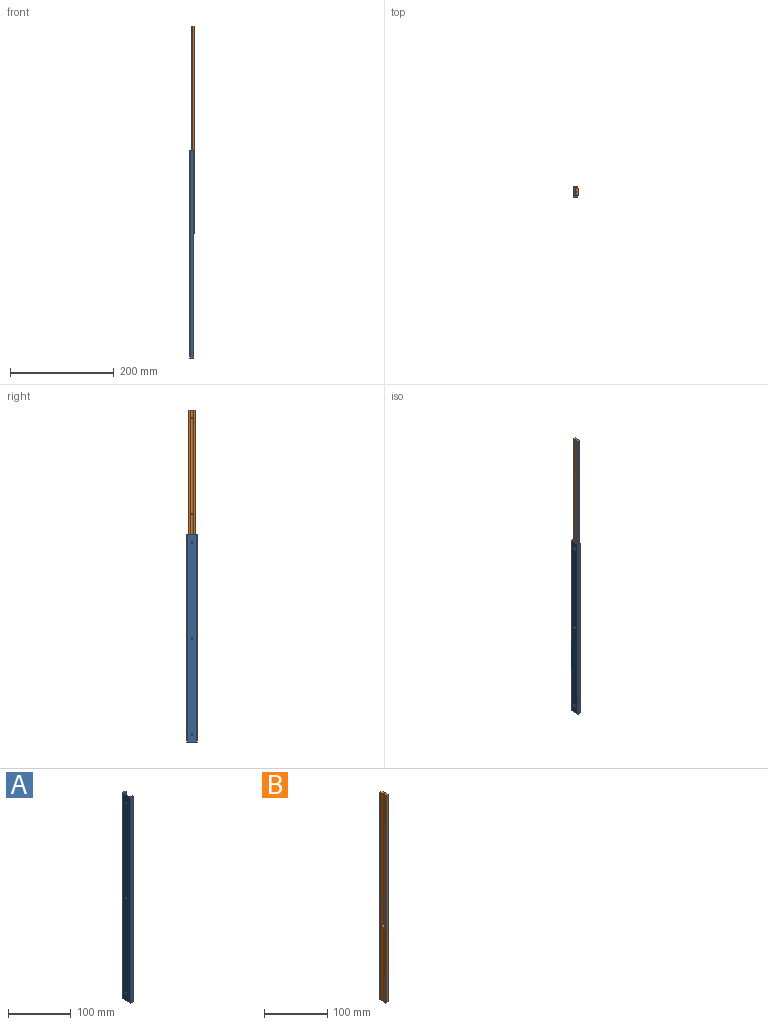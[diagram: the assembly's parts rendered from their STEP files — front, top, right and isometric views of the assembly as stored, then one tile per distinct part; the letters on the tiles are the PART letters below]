
ASSEMBLY  parts=2 mates=1
PART A: 163 faces, bbox 7.6x20.2x400.2 mm
  f0: sphere r=1.2mm, area 2.1mm2, adj f72,f125,f160,f161
  f1: sphere r=1.2mm, area 2.1mm2, adj f72,f125,f158,f159
  f2: sphere r=1.2mm, area 2.1mm2, adj f72,f125,f157,f158
  f3: sphere r=1.2mm, area 2.1mm2, adj f72,f125,f156,f157
  f4: sphere r=1.2mm, area 2.1mm2, adj f72,f125,f155,f156
  f5: sphere r=1.2mm, area 2.1mm2, adj f72,f125,f154,f155
  f6: sphere r=1.2mm, area 2.1mm2, adj f72,f125,f153,f154
  f7: sphere r=1.2mm, area 2.1mm2, adj f72,f125,f152,f153
  f8: sphere r=1.2mm, area 2.1mm2, adj f72,f125,f151,f152
  f9: sphere r=1.2mm, area 2.1mm2, adj f72,f125,f150,f151
  f10: sphere r=1.2mm, area 2.1mm2, adj f72,f125,f149,f150
  f11: sphere r=1.2mm, area 2.1mm2, adj f72,f125,f148,f149
  f12: sphere r=1.2mm, area 2.1mm2, adj f72,f125,f147,f148
  f13: sphere r=1.2mm, area 2.1mm2, adj f72,f125,f146,f147
  f14: sphere r=1.2mm, area 2.1mm2, adj f72,f125,f145,f146
  f15: sphere r=1.2mm, area 2.1mm2, adj f72,f125,f144,f145
  f16: sphere r=1.2mm, area 2.1mm2, adj f72,f125,f143,f144
  f17: sphere r=1.2mm, area 2.1mm2, adj f72,f125,f142,f143
  f18: sphere r=1.2mm, area 2.1mm2, adj f72,f125,f141,f142
  f19: sphere r=1.2mm, area 2.1mm2, adj f72,f125,f140,f141
  f20: sphere r=1.2mm, area 2.1mm2, adj f72,f125,f139,f140
  f21: sphere r=1.2mm, area 2.1mm2, adj f72,f125,f138,f139
  f22: sphere r=1.2mm, area 2.1mm2, adj f72,f125,f137,f138
  f23: sphere r=1.2mm, area 2.1mm2, adj f72,f125,f136,f137
  f24: sphere r=1.2mm, area 2.1mm2, adj f72,f125,f135,f136
  f25: sphere r=1.2mm, area 2.1mm2, adj f72,f125,f134,f135
  f26: sphere r=1.2mm, area 2.1mm2, adj f72,f125,f133,f134
  f27: sphere r=1.2mm, area 2.1mm2, adj f72,f125,f132,f133
  f28: sphere r=1.2mm, area 2.1mm2, adj f72,f125,f131,f132
  f29: sphere r=1.2mm, area 2.1mm2, adj f72,f125,f130,f131
  f30: sphere r=1.2mm, area 2.1mm2, adj f72,f125,f129,f130
  f31: sphere r=1.2mm, area 2.1mm2, adj f72,f125,f128,f129
  f32: sphere r=1.2mm, area 2.1mm2, adj f72,f125,f127,f128
  f33: sphere r=1.2mm, area 2.1mm2, adj f72,f125,f126,f127
  f34: sphere r=1.2mm, area 2.1mm2, adj f72,f125,f126,f160
  f35: sphere r=1.2mm, area 2.1mm2, adj f77,f83,f119,f120
  f36: sphere r=1.2mm, area 2.1mm2, adj f77,f83,f117,f118
  f37: sphere r=1.2mm, area 2.1mm2, adj f77,f83,f116,f117
  f38: sphere r=1.2mm, area 2.1mm2, adj f77,f83,f115,f116
  f39: sphere r=1.2mm, area 2.1mm2, adj f77,f83,f114,f115
  f40: sphere r=1.2mm, area 2.1mm2, adj f77,f83,f113,f114
  f41: sphere r=1.2mm, area 2.1mm2, adj f77,f83,f112,f113
  f42: sphere r=1.2mm, area 2.1mm2, adj f77,f83,f111,f112
  f43: sphere r=1.2mm, area 2.1mm2, adj f77,f83,f110,f111
  f44: sphere r=1.2mm, area 2.1mm2, adj f77,f83,f109,f110
  f45: sphere r=1.2mm, area 2.1mm2, adj f77,f83,f108,f109
  f46: sphere r=1.2mm, area 2.1mm2, adj f77,f83,f107,f108
  f47: sphere r=1.2mm, area 2.1mm2, adj f77,f83,f106,f107
  f48: sphere r=1.2mm, area 2.1mm2, adj f77,f83,f105,f106
  f49: sphere r=1.2mm, area 2.1mm2, adj f77,f83,f104,f105
  f50: sphere r=1.2mm, area 2.1mm2, adj f77,f83,f103,f104
  f51: sphere r=1.2mm, area 2.1mm2, adj f77,f83,f102,f103
  f52: sphere r=1.2mm, area 2.1mm2, adj f77,f83,f101,f102
  f53: sphere r=1.2mm, area 2.1mm2, adj f77,f83,f100,f101
  f54: sphere r=1.2mm, area 2.1mm2, adj f77,f83,f99,f100
  f55: sphere r=1.2mm, area 2.1mm2, adj f77,f83,f98,f99
  f56: sphere r=1.2mm, area 2.1mm2, adj f77,f83,f97,f98
  f57: sphere r=1.2mm, area 2.1mm2, adj f77,f83,f96,f97
  f58: sphere r=1.2mm, area 2.1mm2, adj f77,f83,f95,f96
  f59: sphere r=1.2mm, area 2.1mm2, adj f77,f83,f94,f95
  f60: sphere r=1.2mm, area 2.1mm2, adj f77,f83,f93,f94
  f61: sphere r=1.2mm, area 2.1mm2, adj f77,f83,f92,f93
  f62: sphere r=1.2mm, area 2.1mm2, adj f77,f83,f91,f92
  f63: sphere r=1.2mm, area 2.1mm2, adj f77,f83,f90,f91
  f64: sphere r=1.2mm, area 2.1mm2, adj f77,f83,f89,f90
  f65: sphere r=1.2mm, area 2.1mm2, adj f77,f83,f88,f89
  f66: sphere r=1.2mm, area 2.1mm2, adj f77,f83,f87,f88
  f67: sphere r=1.2mm, area 2.1mm2, adj f77,f83,f86,f87
  f68: sphere r=1.2mm, area 2.1mm2, adj f77,f83,f85,f86
  f69: sphere r=1.2mm, area 2.1mm2, adj f77,f83,f84,f85
  f70: sphere r=1.2mm, area 2.1mm2, adj f77,f83,f84,f119
  f71: sphere r=1.2mm, area 2.1mm2, adj f72,f125,f159,f162
  f72: plane 400.25x1.51mm, normal (0,1,0), area 504mm2, adj f0,f1,f2,f3,f4,f5,f6,f7
  f73: plane 20x7.4mm, normal (0,0,1), area 56.3mm2, adj f72,f74,f75,f76,f77,f79,f80,f82
  f74: plane 400x0.71mm, normal (-0.71,0.71,0), area 400mm2, adj f73,f75,f78,f80
  f75: plane 400x6.69mm, normal (0,1,0), area 2677.2mm2, adj f73,f74,f76,f78
  f76: plane 400x2.5mm, normal (1,0,0), area 1000mm2, adj f73,f75,f77,f78
  f77: plane 400.25x3.11mm, normal (0,-1,0), area 1144mm2, adj f35,f36,f37,f38,f39,f40,f41,f42
  f78: plane 20x7.4mm, normal (0,0,-1), area 56.3mm2, adj f72,f74,f75,f76,f77,f79,f80,f82
  f79: plane 400x0.71mm, normal (-0.71,-0.71,0), area 400mm2, adj f73,f78,f80,f123
  f80: plane 400x18.59mm, normal (-1,0,0), area 7408.7mm2, adj f73,f74,f78,f79,f81,f121,f122
  f81: cone r=1.65mm half-angle=45deg, axis (1,0,0), area 29.2mm2, adj f80,f82
  f82: plane 400x15mm, normal (1,0,0), area 5912.3mm2, adj f72,f73,f78,f81,f83,f121,f122
  f83: plane 400.25x1.51mm, normal (0,-1,0), area 504mm2, adj f35,f36,f37,f38,f39,f40,f41,f42
  f84: cylinder r=1.2mm len=2.51mm, axis (0,0,1), area 5.2mm2, adj f69,f70,f77,f83
  f85: cylinder r=1.2mm len=2.51mm, axis (0,0,1), area 5.2mm2, adj f68,f69,f77,f83
  f86: cylinder r=1.2mm len=2.51mm, axis (0,0,1), area 5.2mm2, adj f67,f68,f77,f83
  f87: cylinder r=1.2mm len=2.51mm, axis (0,0,1), area 5.2mm2, adj f66,f67,f77,f83
  f88: cylinder r=1.2mm len=2.51mm, axis (0,0,1), area 5.2mm2, adj f65,f66,f77,f83
  f89: cylinder r=1.2mm len=2.51mm, axis (0,0,1), area 5.2mm2, adj f64,f65,f77,f83
  f90: cylinder r=1.2mm len=2.51mm, axis (0,0,1), area 5.2mm2, adj f63,f64,f77,f83
  f91: cylinder r=1.2mm len=2.51mm, axis (0,0,1), area 5.2mm2, adj f62,f63,f77,f83
  f92: cylinder r=1.2mm len=2.51mm, axis (0,0,1), area 5.2mm2, adj f61,f62,f77,f83
  f93: cylinder r=1.2mm len=2.51mm, axis (0,0,1), area 5.2mm2, adj f60,f61,f77,f83
  f94: cylinder r=1.2mm len=2.51mm, axis (0,0,1), area 5.2mm2, adj f59,f60,f77,f83
  f95: cylinder r=1.2mm len=2.51mm, axis (0,0,1), area 5.2mm2, adj f58,f59,f77,f83
  f96: cylinder r=1.2mm len=2.51mm, axis (0,0,1), area 5.2mm2, adj f57,f58,f77,f83
  f97: cylinder r=1.2mm len=2.51mm, axis (0,0,1), area 5.2mm2, adj f56,f57,f77,f83
  f98: cylinder r=1.2mm len=2.51mm, axis (0,0,1), area 5.2mm2, adj f55,f56,f77,f83
  f99: cylinder r=1.2mm len=2.51mm, axis (0,0,1), area 5.2mm2, adj f54,f55,f77,f83
  f100: cylinder r=1.2mm len=2.51mm, axis (0,0,1), area 5.2mm2, adj f53,f54,f77,f83
  f101: cylinder r=1.2mm len=2.51mm, axis (0,0,1), area 5.2mm2, adj f52,f53,f77,f83
  f102: cylinder r=1.2mm len=2.51mm, axis (0,0,1), area 5.2mm2, adj f51,f52,f77,f83
  f103: cylinder r=1.2mm len=2.51mm, axis (0,0,1), area 5.2mm2, adj f50,f51,f77,f83
  f104: cylinder r=1.2mm len=2.51mm, axis (0,0,1), area 5.2mm2, adj f49,f50,f77,f83
  f105: cylinder r=1.2mm len=2.51mm, axis (0,0,1), area 5.2mm2, adj f48,f49,f77,f83
  f106: cylinder r=1.2mm len=2.51mm, axis (0,0,1), area 5.2mm2, adj f47,f48,f77,f83
  f107: cylinder r=1.2mm len=2.51mm, axis (0,0,1), area 5.2mm2, adj f46,f47,f77,f83
  f108: cylinder r=1.2mm len=2.51mm, axis (0,0,1), area 5.2mm2, adj f45,f46,f77,f83
  f109: cylinder r=1.2mm len=2.51mm, axis (0,0,1), area 5.2mm2, adj f44,f45,f77,f83
  f110: cylinder r=1.2mm len=2.51mm, axis (0,0,1), area 5.2mm2, adj f43,f44,f77,f83
  f111: cylinder r=1.2mm len=2.51mm, axis (0,0,1), area 5.2mm2, adj f42,f43,f77,f83
  f112: cylinder r=1.2mm len=2.51mm, axis (0,0,1), area 5.2mm2, adj f41,f42,f77,f83
  f113: cylinder r=1.2mm len=2.51mm, axis (0,0,1), area 5.2mm2, adj f40,f41,f77,f83
  f114: cylinder r=1.2mm len=2.51mm, axis (0,0,1), area 5.2mm2, adj f39,f40,f77,f83
  f115: cylinder r=1.2mm len=2.51mm, axis (0,0,1), area 5.2mm2, adj f38,f39,f77,f83
  f116: cylinder r=1.2mm len=2.51mm, axis (0,0,1), area 5.2mm2, adj f37,f38,f77,f83
  f117: cylinder r=1.2mm len=2.51mm, axis (0,0,1), area 5.2mm2, adj f36,f37,f77,f83
  f118: cylinder r=1.2mm len=142.58mm, axis (0,0,1), area 306.4mm2, adj f36,f77,f78,f83
  f119: cylinder r=1.2mm len=2.51mm, axis (0,0,1), area 5.2mm2, adj f35,f70,f77,f83
  f120: cylinder r=1.2mm len=142.58mm, axis (0,0,1), area 306.4mm2, adj f35,f73,f77,f83
  f121: cone r=1.65mm half-angle=45deg, axis (1,0,0), area 29.2mm2, adj f80,f82
  f122: cone r=1.65mm half-angle=45deg, axis (1,0,0), area 29.2mm2, adj f80,f82
  f123: plane 400x6.69mm, normal (0,-1,0), area 2677.2mm2, adj f73,f78,f79,f124
  f124: plane 400x2.5mm, normal (1,0,0), area 1000mm2, adj f73,f78,f123,f125
  f125: plane 400.25x3.11mm, normal (0,1,0), area 1144mm2, adj f0,f1,f2,f3,f4,f5,f6,f7
  f126: cylinder r=1.2mm len=2.51mm, axis (0,0,1), area 5.2mm2, adj f33,f34,f72,f125
  f127: cylinder r=1.2mm len=2.51mm, axis (0,0,1), area 5.2mm2, adj f32,f33,f72,f125
  f128: cylinder r=1.2mm len=2.51mm, axis (0,0,1), area 5.2mm2, adj f31,f32,f72,f125
  f129: cylinder r=1.2mm len=2.51mm, axis (0,0,1), area 5.2mm2, adj f30,f31,f72,f125
  f130: cylinder r=1.2mm len=2.51mm, axis (0,0,1), area 5.2mm2, adj f29,f30,f72,f125
  f131: cylinder r=1.2mm len=2.51mm, axis (0,0,1), area 5.2mm2, adj f28,f29,f72,f125
  f132: cylinder r=1.2mm len=2.51mm, axis (0,0,1), area 5.2mm2, adj f27,f28,f72,f125
  f133: cylinder r=1.2mm len=2.51mm, axis (0,0,1), area 5.2mm2, adj f26,f27,f72,f125
  f134: cylinder r=1.2mm len=2.51mm, axis (0,0,1), area 5.2mm2, adj f25,f26,f72,f125
  f135: cylinder r=1.2mm len=2.51mm, axis (0,0,1), area 5.2mm2, adj f24,f25,f72,f125
  f136: cylinder r=1.2mm len=2.51mm, axis (0,0,1), area 5.2mm2, adj f23,f24,f72,f125
  f137: cylinder r=1.2mm len=2.51mm, axis (0,0,1), area 5.2mm2, adj f22,f23,f72,f125
  f138: cylinder r=1.2mm len=2.51mm, axis (0,0,1), area 5.2mm2, adj f21,f22,f72,f125
  f139: cylinder r=1.2mm len=2.51mm, axis (0,0,1), area 5.2mm2, adj f20,f21,f72,f125
  f140: cylinder r=1.2mm len=2.51mm, axis (0,0,1), area 5.2mm2, adj f19,f20,f72,f125
  f141: cylinder r=1.2mm len=2.51mm, axis (0,0,1), area 5.2mm2, adj f18,f19,f72,f125
  f142: cylinder r=1.2mm len=2.51mm, axis (0,0,1), area 5.2mm2, adj f17,f18,f72,f125
  f143: cylinder r=1.2mm len=2.51mm, axis (0,0,1), area 5.2mm2, adj f16,f17,f72,f125
  f144: cylinder r=1.2mm len=2.51mm, axis (0,0,1), area 5.2mm2, adj f15,f16,f72,f125
  f145: cylinder r=1.2mm len=2.51mm, axis (0,0,1), area 5.2mm2, adj f14,f15,f72,f125
  f146: cylinder r=1.2mm len=2.51mm, axis (0,0,1), area 5.2mm2, adj f13,f14,f72,f125
  f147: cylinder r=1.2mm len=2.51mm, axis (0,0,1), area 5.2mm2, adj f12,f13,f72,f125
  f148: cylinder r=1.2mm len=2.51mm, axis (0,0,1), area 5.2mm2, adj f11,f12,f72,f125
  f149: cylinder r=1.2mm len=2.51mm, axis (0,0,1), area 5.2mm2, adj f10,f11,f72,f125
  f150: cylinder r=1.2mm len=2.51mm, axis (0,0,1), area 5.2mm2, adj f9,f10,f72,f125
  f151: cylinder r=1.2mm len=2.51mm, axis (0,0,1), area 5.2mm2, adj f8,f9,f72,f125
  f152: cylinder r=1.2mm len=2.51mm, axis (0,0,1), area 5.2mm2, adj f7,f8,f72,f125
  f153: cylinder r=1.2mm len=2.51mm, axis (0,0,1), area 5.2mm2, adj f6,f7,f72,f125
  f154: cylinder r=1.2mm len=2.51mm, axis (0,0,1), area 5.2mm2, adj f5,f6,f72,f125
  f155: cylinder r=1.2mm len=2.51mm, axis (0,0,1), area 5.2mm2, adj f4,f5,f72,f125
  f156: cylinder r=1.2mm len=2.51mm, axis (0,0,1), area 5.2mm2, adj f3,f4,f72,f125
  f157: cylinder r=1.2mm len=2.51mm, axis (0,0,1), area 5.2mm2, adj f2,f3,f72,f125
  f158: cylinder r=1.2mm len=2.51mm, axis (0,0,1), area 5.2mm2, adj f1,f2,f72,f125
  f159: cylinder r=1.2mm len=2.51mm, axis (0,0,1), area 5.2mm2, adj f1,f71,f72,f125
  f160: cylinder r=1.2mm len=2.51mm, axis (0,0,1), area 5.2mm2, adj f0,f34,f72,f125
  f161: cylinder r=1.2mm len=142.58mm, axis (0,0,1), area 306.4mm2, adj f0,f72,f73,f125
  f162: cylinder r=1.2mm len=142.58mm, axis (0,0,1), area 306.4mm2, adj f71,f72,f78,f125
PART B: 27 faces, bbox 5.8x12.1x400 mm
  f0: cylinder r=1.62mm len=3.74mm, axis (-1,0,0), area 37.3mm2, adj f1,f24,f25,f26
  f1: cone r=1.62mm half-angle=45deg, axis (1,0,0), area 6.1mm2, adj f0,f2
  f2: plane 400x12.1mm, normal (1,0,0), area 4763.8mm2, adj f1,f3,f18,f19,f20,f21,f22,f23
  f3: cone r=1.62mm half-angle=45deg, axis (1,0,0), area 6.1mm2, adj f2,f4
  f4: cylinder r=1.62mm len=3.74mm, axis (-1,0,0), area 37.3mm2, adj f3,f5,f6,f17
  f5: cone r=2mm half-angle=45deg, axis (-1,0,0), area 0mm2, adj f4,f6
  f6: cylinder r=3.4mm len=253.95mm, axis (0,0,1), area 1925.6mm2, adj f4,f5,f7,f8,f9,f10,f13,f14
  f7: cone r=2mm half-angle=45deg, axis (-1,0,0), area 0mm2, adj f6,f9
  f8: cone r=2mm half-angle=45deg, axis (-1,0,0), area 0mm2, adj f6,f9
  f9: cylinder r=1.62mm len=3.74mm, axis (-1,0,0), area 37.3mm2, adj f6,f7,f8,f18
  f10: plane 400x2.97mm, normal (-1,0,0), area 1189.6mm2, adj f6,f11,f13,f21,f23,f25
  f11: plane 400x0.31mm, normal (0,1,0), area 122.2mm2, adj f10,f12,f21,f23
  f12: cylinder r=1.2mm len=400mm, axis (0,0,1), area 807.4mm2, adj f11,f21,f22,f23
  f13: cylinder r=3.25mm len=6.5mm, axis (-1,0,0), area 97.6mm2, adj f6,f10,f14,f19,f25
  f14: plane 400x2.97mm, normal (-1,0,0), area 1189.6mm2, adj f6,f13,f15,f21,f23,f25
  f15: plane 400x0.31mm, normal (0,-1,0), area 122.2mm2, adj f14,f16,f21,f23
  f16: cylinder r=1.2mm len=400mm, axis (0,0,1), area 807.4mm2, adj f15,f20,f21,f23
  f17: cone r=2mm half-angle=45deg, axis (-1,0,0), area 0mm2, adj f4,f6
  f18: cone r=1.62mm half-angle=45deg, axis (1,0,0), area 6.1mm2, adj f2,f9
  f19: cone r=3.25mm half-angle=45deg, axis (1,0,0), area 7.5mm2, adj f2,f13
  f20: plane 400x3.71mm, normal (0,-1,0), area 1482.2mm2, adj f2,f16,f21,f23
  f21: plane 12.1x5.8mm, normal (0,0,1), area 60.6mm2, adj f2,f6,f10,f11,f12,f14,f15,f16
  f22: plane 400x3.71mm, normal (0,1,0), area 1482.2mm2, adj f2,f12,f21,f23
  f23: plane 12.1x5.8mm, normal (0,0,-1), area 60.6mm2, adj f2,f10,f11,f12,f14,f15,f16,f20
  f24: cone r=2mm half-angle=45deg, axis (-1,0,0), area 0mm2, adj f0,f25
  f25: cylinder r=3.4mm len=143.95mm, axis (0,0,1), area 1089mm2, adj f0,f10,f13,f14,f23,f24,f26
  f26: cone r=2mm half-angle=45deg, axis (-1,0,0), area 0mm2, adj f0,f25
PLACE A t=(5,-3.95,25.94)mm fixed
PLACE B t=(0,0.1,265.94)mm
MATE slider B.f16 <-> A.f126  axis (0,0,1) through (1.2,-0.7,665.94)mm
